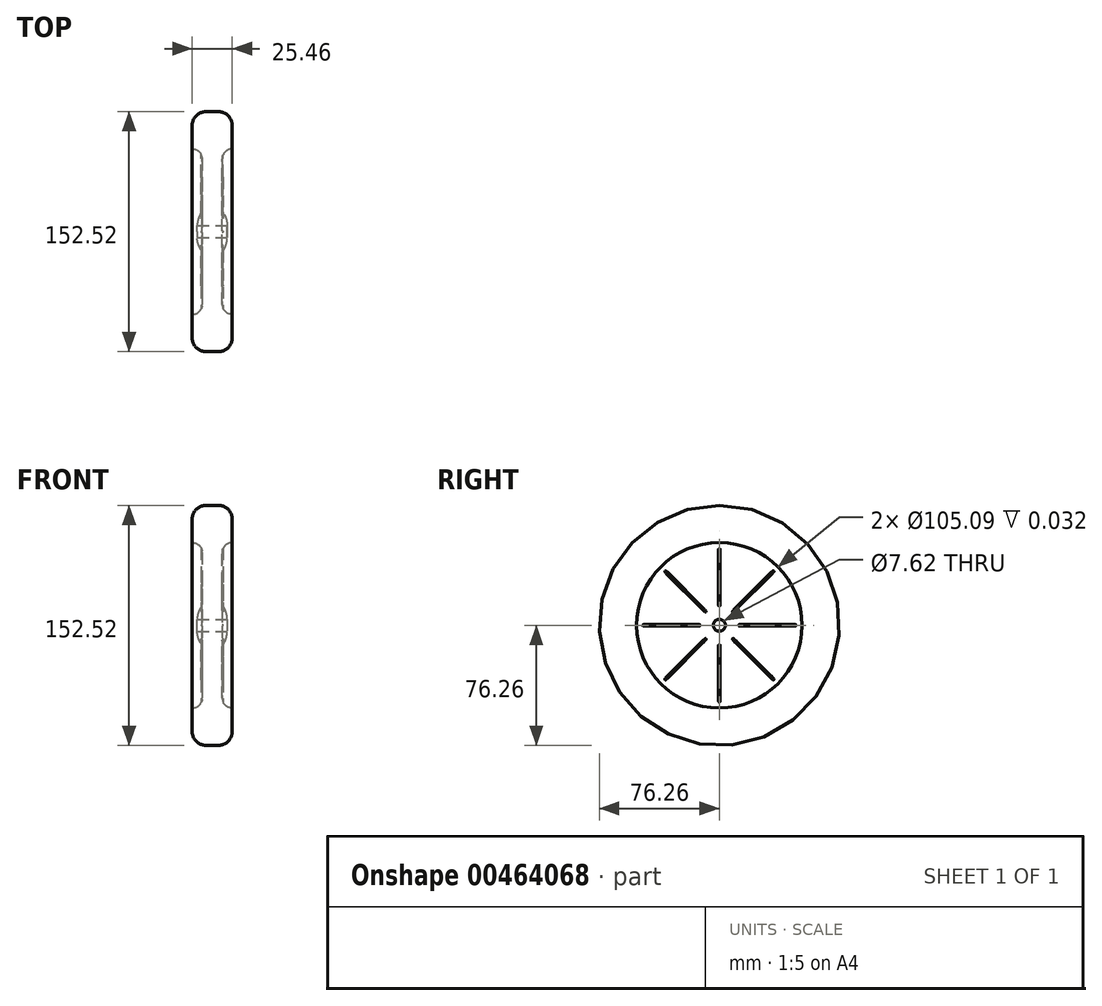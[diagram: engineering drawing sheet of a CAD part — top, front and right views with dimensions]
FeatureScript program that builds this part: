
annotation { "Feature Type Name" : "Feature", "Feature Type Description" : "" }
export const myFeature = defineFeature(function(context is Context, id is Id, definition is map)
    precondition{}
    {
        {
            var Q0;
            Q0=qCreatedBy(makeId("Top.planeOp"),FACE);
            var sketch = newSketch(context, id + "F0", { "sketchPlane" : qUnion([Q0])});
            skLineSegment(sketch, "E0", {"start": v(-6.3, -52.55) * mm, "end": v(-6.3, -12.74) * mm});
            skLineSegment(sketch, "E1", {"start": v(6.35, -12.7) * mm, "end": v(6.35, -52.55) * mm});
            skLineSegment(sketch, "E2", {"start": v(-9.53, 0) * mm, "end": v(-9.53, -3.81) * mm});
            skArc(sketch, "E3", {"start": v(-9.53, -3.81) * mm, "mid": v(-8.7, -8.56) * mm, "end": v(-6.3, -12.74) * mm});
            skArc(sketch, "E4", {"start": v(-12.7, 0) * mm, "mid": v(-11.82, -2.5) * mm, "end": v(-9.53, -3.8) * mm});
            skArc(sketch, "E5.MirrorCS", {"start": v(9.53, -3.81) * mm, "mid": v(8.7, -8.53) * mm, "end": v(6.35, -12.7) * mm});
            skArc(sketch, "E6.MirrorCS", {"start": v(12.7, 0) * mm, "mid": v(11.82, -2.5) * mm, "end": v(9.53, -3.8) * mm});
            skLineSegment(sketch, "E7", {"start": v(-12.7, 0) * mm, "end": v(12.7, 0) * mm});
            skLineSegment(sketch, "E8", {"start": v(12.73, -63.55) * mm, "end": v(12.73, -52.55) * mm});
            skLineSegment(sketch, "E9", {"start": v(12.73, -52.55) * mm, "end": v(6.35, -52.55) * mm});
            skLineSegment(sketch, "E10", {"start": v(12.73, -63.55) * mm, "end": v(12.73, -76.26) * mm});
            skLineSegment(sketch, "E11", {"start": v(-6.3, -52.55) * mm, "end": v(-12.73, -52.55) * mm});
            skLineSegment(sketch, "E12", {"start": v(-12.73, -52.55) * mm, "end": v(-12.73, -76.24) * mm});
            skLineSegment(sketch, "E13", {"start": v(-12.73, -76.24) * mm, "end": v(12.73, -76.26) * mm});
            skSolve(sketch);
        }
        {
            var Q0;
            Q0=makeQuery(id+"F0.imprint","IMPRINT",FACE,{"disambiguationData":[TD([[makeQuery(id+"F0.imprint","IMPRINT",EDGE,{"derivedFrom":sQuery(id+"F0.wireOp",EDGE,"E0")}),-1.0]])]});
            var Q1;
            {var subQ0=sQuery(id+"F0.wireOp",EDGE,"6V25OecG-Z0nX-RHxG-JKtg-aJSisBqB9ty6");var subQ1=makeQuery(id+"F0.imprint","INTERSECT",VERTEX,{"derivedFrom":[subQ0,sQuery(id+"F0.wireOp",EDGE,"s2MWHd5B-Butg-I8NC-5foa-pCvdFhJTHkwg")]});Q1=makeQuery(id+"F0.imprint","IMPRINT",FACE,{"disambiguationData":[TD([[makeQuery(id+"F0.imprint","IMPRINT",EDGE,{"disambiguationData":[TD([[subQ1,1.0]])],"derivedFrom":subQ0}),1.0]])]});}
            var Q2;
            Q2=makeQuery(id+"F0.imprint","IMPRINT",FACE,{"disambiguationData":[TD([[makeQuery(id+"F0.imprint","IMPRINT",EDGE,{"derivedFrom":sQuery(id+"F0.wireOp",EDGE,"wWwMu1eG-bIHq-Cr3w-0RTv-qLqCbcrmc8dO")}),1.0]])]});
            var Q3;
            Q3=makeQuery(id+"F0.imprint","IMPRINT",FACE,{"disambiguationData":[TD([[makeQuery(id+"F0.imprint","IMPRINT",EDGE,{"derivedFrom":sQuery(id+"F0.wireOp",EDGE,"6V25OecG-Z0nX-RHxG-JKtg-aJSisBqB9ty6")}),1.0]])]});
            var Q4;
            {var subQ0=sQuery(id+"F0.wireOp",EDGE,"E2");Q4=makeQuery(id+"F0.imprint","IMPRINT",FACE,{"disambiguationData":[TD([[makeQuery(id+"F0.imprint","IMPRINT",EDGE,{"derivedFrom":subQ0}),-1.0]])]});}
            var Q5;
            Q5=sQuery(id+"F0.wireOp",EDGE,"E7");
            revolve(context, id + "F1", {"entities" : qUnion([Q0, Q1, Q2, Q3, Q4]), "axis" : qUnion([Q5]), "revolveType" : RevolveType.FULL});
        }
        {
            var Q0;
            Q0=makeQuery(id+"F1.opRevolve","SWEPT_EDGE",EDGE,{"disambiguationData":[OSD([sQuery(id+"F0.wireOp",EDGE,"6V25OecG-Z0nX-RHxG-JKtg-aJSisBqB9ty6"),sQuery(id+"F0.wireOp",EDGE,"E1")])]});
            var Q1;
            Q1=makeQuery(id+"F1.opRevolve","SWEPT_EDGE",EDGE,{"disambiguationData":[OSD([sQuery(id+"F0.wireOp",EDGE,"6V25OecG-Z0nX-RHxG-JKtg-aJSisBqB9ty6"),sQuery(id+"F0.wireOp",EDGE,"E0")])]});
            fillet(context, id + "F2", {"entities" : qUnion([Q0, Q1]), "radius" : 6.35 * mm, "tangentPropagation" : true, "allowEdgeOverflow" : false});
        }
        {
            var Q0;
            Q0=makeQuery(id+"F1.opRevolve","SWEPT_FACE",FACE,{"disambiguationData":[OSD([sQuery(id+"F0.wireOp",EDGE,"E0")])]});
            var sketch = newSketch(context, id + "F3", { "sketchPlane" : qUnion([Q0])});
            skLineSegment(sketch, "E14", {"start": v(0, 0) * mm, "end": v(-46.2, 0) * mm});
            skLineSegment(sketch, "E15", {"start": v(0, 0) * mm, "end": v(0, 0.5) * mm});
            skLineSegment(sketch, "E16", {"start": v(-46.2, 0.5) * mm, "end": v(-46.2, 0) * mm});
            skLineSegment(sketch, "E17.MirrorCS", {"start": v(0, -0.5) * mm, "end": v(-46.2, -0.5) * mm});
            skLineSegment(sketch, "E18.MirrorCS", {"start": v(-46.2, -0.5) * mm, "end": v(-46.2, 0) * mm});
            skLineSegment(sketch, "E19.MirrorCS", {"start": v(0, 0) * mm, "end": v(0, -0.5) * mm});
            skLineSegment(sketch, "E20.1.4", {"start": v(0, 0) * mm, "end": v(-0.36, 0.36) * mm});
            skLineSegment(sketch, "E20.1.5", {"start": v(0, 0) * mm, "end": v(0.36, -0.36) * mm});
            skLineSegment(sketch, "E20.2.4", {"start": v(0, 0) * mm, "end": v(-0.5, 0) * mm});
            skLineSegment(sketch, "E20.2.5", {"start": v(0, 0) * mm, "end": v(0.5, 0) * mm});
            skLineSegment(sketch, "E20.3.4", {"start": v(0, 0) * mm, "end": v(-0.36, -0.36) * mm});
            skLineSegment(sketch, "E20.3.5", {"start": v(0, 0) * mm, "end": v(0.36, 0.36) * mm});
            skLineSegment(sketch, "E20.5.4", {"start": v(0, 0) * mm, "end": v(0.36, -0.36) * mm});
            skLineSegment(sketch, "E20.5.5", {"start": v(0, 0) * mm, "end": v(-0.36, 0.36) * mm});
            skLineSegment(sketch, "E20.6.4", {"start": v(0, 0) * mm, "end": v(0.5, 0) * mm});
            skLineSegment(sketch, "E20.6.5", {"start": v(0, 0) * mm, "end": v(-0.5, 0) * mm});
            skLineSegment(sketch, "E20.7.4", {"start": v(0, 0) * mm, "end": v(0.36, 0.36) * mm});
            skLineSegment(sketch, "E20.7.5", {"start": v(0, 0) * mm, "end": v(-0.36, -0.36) * mm});
            skPoint(sketch, "E20.center", {"position": v(0, 0) * mm});
            skLineSegment(sketch, "E21", {"start": v(0, 0.5) * mm, "end": v(-49.43, 0.5) * mm});
            skLineSegment(sketch, "E22", {"start": v(-49.43, 0.5) * mm, "end": v(-49.43, -0.5) * mm});
            skLineSegment(sketch, "E23", {"start": v(-49.43, -0.5) * mm, "end": v(-46.2, -0.5) * mm});
            skLineSegment(sketch, "E24.1.0", {"start": v(-0.36, 0.36) * mm, "end": v(-35.31, -34.6) * mm});
            skLineSegment(sketch, "E24.1.1", {"start": v(0.36, -0.36) * mm, "end": v(-32.3, -33.02) * mm});
            skLineSegment(sketch, "E24.1.2", {"start": v(-34.6, -35.31) * mm, "end": v(-32.3, -33.02) * mm});
            skLineSegment(sketch, "E24.1.3", {"start": v(-35.31, -34.6) * mm, "end": v(-34.6, -35.31) * mm});
            skLineSegment(sketch, "E24.2.0", {"start": v(-0.5, 0) * mm, "end": v(-0.5, -49.43) * mm});
            skLineSegment(sketch, "E24.2.1", {"start": v(0.5, 0) * mm, "end": v(0.5, -46.2) * mm});
            skLineSegment(sketch, "E24.2.2", {"start": v(0.5, -49.43) * mm, "end": v(0.5, -46.2) * mm});
            skLineSegment(sketch, "E24.2.3", {"start": v(-0.5, -49.43) * mm, "end": v(0.5, -49.43) * mm});
            skLineSegment(sketch, "E24.3.0", {"start": v(-0.36, -0.36) * mm, "end": v(34.6, -35.31) * mm});
            skLineSegment(sketch, "E24.3.1", {"start": v(0.36, 0.36) * mm, "end": v(33.02, -32.3) * mm});
            skLineSegment(sketch, "E24.3.2", {"start": v(35.31, -34.6) * mm, "end": v(33.02, -32.3) * mm});
            skLineSegment(sketch, "E24.3.3", {"start": v(34.6, -35.31) * mm, "end": v(35.31, -34.6) * mm});
            skLineSegment(sketch, "E24.4.0", {"start": v(0, -0.5) * mm, "end": v(49.43, -0.5) * mm});
            skLineSegment(sketch, "E24.4.1", {"start": v(0, 0.5) * mm, "end": v(46.2, 0.5) * mm});
            skLineSegment(sketch, "E24.4.2", {"start": v(49.43, 0.5) * mm, "end": v(46.2, 0.5) * mm});
            skLineSegment(sketch, "E24.4.3", {"start": v(49.43, -0.5) * mm, "end": v(49.43, 0.5) * mm});
            skLineSegment(sketch, "E24.5.0", {"start": v(0.36, -0.36) * mm, "end": v(35.31, 34.6) * mm});
            skLineSegment(sketch, "E24.5.1", {"start": v(-0.36, 0.36) * mm, "end": v(32.3, 33.02) * mm});
            skLineSegment(sketch, "E24.5.2", {"start": v(34.6, 35.31) * mm, "end": v(32.3, 33.02) * mm});
            skLineSegment(sketch, "E24.5.3", {"start": v(35.31, 34.6) * mm, "end": v(34.6, 35.31) * mm});
            skLineSegment(sketch, "E24.6.0", {"start": v(0.5, 0) * mm, "end": v(0.5, 49.43) * mm});
            skLineSegment(sketch, "E24.6.1", {"start": v(-0.5, 0) * mm, "end": v(-0.5, 46.2) * mm});
            skLineSegment(sketch, "E24.6.2", {"start": v(-0.5, 49.43) * mm, "end": v(-0.5, 46.2) * mm});
            skLineSegment(sketch, "E24.6.3", {"start": v(0.5, 49.43) * mm, "end": v(-0.5, 49.43) * mm});
            skLineSegment(sketch, "E24.7.0", {"start": v(0.36, 0.36) * mm, "end": v(-34.6, 35.31) * mm});
            skLineSegment(sketch, "E24.7.1", {"start": v(-0.36, -0.36) * mm, "end": v(-33.02, 32.3) * mm});
            skLineSegment(sketch, "E24.7.2", {"start": v(-35.31, 34.6) * mm, "end": v(-33.02, 32.3) * mm});
            skLineSegment(sketch, "E24.7.3", {"start": v(-34.6, 35.31) * mm, "end": v(-35.31, 34.6) * mm});
            skSolve(sketch);
        }
        {
            var Q0;
            Q0 = qSketchRegion(id + "F3", true);
            extrude(context, id + "F4", {"entities" : qUnion([Q0]), "operationType" : NewBodyOperationType.ADD, "depth" : 0.64 * mm, "offsetDistance" : 25.4 * mm});
        }
        {
            var Q0;
            {var subQ0=sQuery(id+"F3.wireOp",EDGE,"E24.7.0");var subQ1=sQuery(id+"F0.wireOp",EDGE,"E0");var subQ2=makeQuery(id+"F1.opRevolve","SWEPT_FACE",FACE,{"disambiguationData":[OSD([subQ1])]});var subQ3=makeQuery(id+"F3.imprint","INTERSECT",VERTEX,{"derivedFrom":[makeQuery(id+"F2.opFillet","BLEND_EDGE",EDGE,{"blendedFrom":[makeQuery(id+"F1.opRevolve","SWEPT_EDGE",EDGE,{"disambiguationData":[OSD([subQ1,sQuery(id+"F0.wireOp",EDGE,"E11")])]}),subQ2],"blendedInto":[subQ2]}),subQ0]});Q0=makeQuery(id+"F4.opExtrude","CAP_EDGE",EDGE,{"disambiguationData":[OSD([subQ0]),TDD([makeQuery(id+"F3.imprint","IMPRINT",EDGE,{"disambiguationData":[TD([[makeQuery(id+"F3.imprint","INTERSECT",VERTEX,{"derivedFrom":[sQuery(id+"F3.wireOp",EDGE,"E24.6.1"),subQ0]}),-1.0]])],"derivedFrom":subQ0}),makeQuery(id+"F3.imprint","IMPRINT",EDGE,{"disambiguationData":[TD([[subQ3,1.0]])],"derivedFrom":subQ0}),makeQuery(id+"F3.imprint","IMPRINT",EDGE,{"disambiguationData":[TD([[makeQuery(id+"F3.imprint","INTERSECT",VERTEX,{"derivedFrom":[subQ0,sQuery(id+"F3.wireOp",EDGE,"E24.7.3")]}),1.0]])],"derivedFrom":subQ0})])],"isStart":false});}
            var Q1;
            {var subQ0=sQuery(id+"F3.wireOp",EDGE,"E24.6.0");var subQ1=sQuery(id+"F0.wireOp",EDGE,"E0");var subQ2=makeQuery(id+"F1.opRevolve","SWEPT_FACE",FACE,{"disambiguationData":[OSD([subQ1])]});var subQ3=makeQuery(id+"F3.imprint","INTERSECT",VERTEX,{"derivedFrom":[makeQuery(id+"F2.opFillet","BLEND_EDGE",EDGE,{"blendedFrom":[makeQuery(id+"F1.opRevolve","SWEPT_EDGE",EDGE,{"disambiguationData":[OSD([subQ1,sQuery(id+"F0.wireOp",EDGE,"E11")])]}),subQ2],"blendedInto":[subQ2]}),subQ0]});Q1=makeQuery(id+"F4.opExtrude","CAP_EDGE",EDGE,{"disambiguationData":[OSD([subQ0]),TDD([makeQuery(id+"F3.imprint","IMPRINT",EDGE,{"disambiguationData":[TD([[makeQuery(id+"F3.imprint","INTERSECT",VERTEX,{"derivedFrom":[sQuery(id+"F3.wireOp",EDGE,"E24.5.1"),subQ0]}),-1.0]])],"derivedFrom":subQ0}),makeQuery(id+"F3.imprint","IMPRINT",EDGE,{"disambiguationData":[TD([[subQ3,1.0]])],"derivedFrom":subQ0}),makeQuery(id+"F3.imprint","IMPRINT",EDGE,{"disambiguationData":[TD([[makeQuery(id+"F3.imprint","INTERSECT",VERTEX,{"derivedFrom":[subQ0,sQuery(id+"F3.wireOp",EDGE,"E24.6.3")]}),1.0]])],"derivedFrom":subQ0})])],"isStart":false});}
            var Q2;
            {var subQ0=sQuery(id+"F3.wireOp",EDGE,"E24.5.0");var subQ1=sQuery(id+"F0.wireOp",EDGE,"E0");var subQ2=makeQuery(id+"F1.opRevolve","SWEPT_FACE",FACE,{"disambiguationData":[OSD([subQ1])]});var subQ3=makeQuery(id+"F3.imprint","INTERSECT",VERTEX,{"derivedFrom":[makeQuery(id+"F2.opFillet","BLEND_EDGE",EDGE,{"blendedFrom":[makeQuery(id+"F1.opRevolve","SWEPT_EDGE",EDGE,{"disambiguationData":[OSD([subQ1,sQuery(id+"F0.wireOp",EDGE,"E11")])]}),subQ2],"blendedInto":[subQ2]}),subQ0]});Q2=makeQuery(id+"F4.opExtrude","CAP_EDGE",EDGE,{"disambiguationData":[OSD([subQ0]),TDD([makeQuery(id+"F3.imprint","IMPRINT",EDGE,{"disambiguationData":[TD([[makeQuery(id+"F3.imprint","INTERSECT",VERTEX,{"derivedFrom":[sQuery(id+"F3.wireOp",EDGE,"E24.4.1"),subQ0]}),-1.0]])],"derivedFrom":subQ0}),makeQuery(id+"F3.imprint","IMPRINT",EDGE,{"disambiguationData":[TD([[subQ3,1.0]])],"derivedFrom":subQ0}),makeQuery(id+"F3.imprint","IMPRINT",EDGE,{"disambiguationData":[TD([[makeQuery(id+"F3.imprint","INTERSECT",VERTEX,{"derivedFrom":[subQ0,sQuery(id+"F3.wireOp",EDGE,"E24.5.3")]}),1.0]])],"derivedFrom":subQ0})])],"isStart":false});}
            var Q3;
            Q3=makeQuery(id+"F4.opExtrude","CAP_EDGE",EDGE,{"disambiguationData":[OSD([sQuery(id+"F3.wireOp",EDGE,"E17.MirrorCS"),sQuery(id+"F3.wireOp",EDGE,"E23")])],"isStart":false});
            var Q4;
            {var subQ0=sQuery(id+"F3.wireOp",EDGE,"E21");var subQ1=sQuery(id+"F0.wireOp",EDGE,"E0");var subQ2=makeQuery(id+"F1.opRevolve","SWEPT_FACE",FACE,{"disambiguationData":[OSD([subQ1])]});var subQ4=makeQuery(id+"F3.imprint","INTERSECT",VERTEX,{"derivedFrom":[makeQuery(id+"F2.opFillet","BLEND_EDGE",EDGE,{"blendedFrom":[makeQuery(id+"F1.opRevolve","SWEPT_EDGE",EDGE,{"disambiguationData":[OSD([subQ1,sQuery(id+"F0.wireOp",EDGE,"E3")])]}),subQ2],"blendedInto":[subQ2]}),subQ0]});Q4=makeQuery(id+"F4.opExtrude","CAP_EDGE",EDGE,{"disambiguationData":[OSD([subQ0]),TDD([makeQuery(id+"F3.imprint","IMPRINT",EDGE,{"disambiguationData":[TD([[makeQuery(id+"F3.imprint","INTERSECT",VERTEX,{"derivedFrom":[subQ0,sQuery(id+"F3.wireOp",EDGE,"E24.7.1")]}),-1.0]])],"derivedFrom":subQ0}),makeQuery(id+"F3.imprint","IMPRINT",EDGE,{"disambiguationData":[TD([[subQ4,-1.0]])],"derivedFrom":subQ0}),makeQuery(id+"F3.imprint","IMPRINT",EDGE,{"disambiguationData":[TD([[makeQuery(id+"F3.imprint","INTERSECT",VERTEX,{"derivedFrom":[subQ0,sQuery(id+"F3.wireOp",EDGE,"E22")]}),1.0]])],"derivedFrom":subQ0})])],"isStart":false});}
            var Q5;
            Q5=makeQuery(id+"F4.opExtrude","CAP_EDGE",EDGE,{"disambiguationData":[OSD([sQuery(id+"F3.wireOp",EDGE,"E24.6.1"),sQuery(id+"F3.wireOp",EDGE,"E24.6.2")])],"isStart":false});
            var Q6;
            Q6=makeQuery(id+"F4.opExtrude","CAP_EDGE",EDGE,{"disambiguationData":[OSD([sQuery(id+"F3.wireOp",EDGE,"E24.5.1"),sQuery(id+"F3.wireOp",EDGE,"E24.5.2")])],"isStart":false});
            var Q7;
            Q7=makeQuery(id+"F4.opExtrude","CAP_EDGE",EDGE,{"disambiguationData":[OSD([sQuery(id+"F3.wireOp",EDGE,"E24.7.1"),sQuery(id+"F3.wireOp",EDGE,"E24.7.2")])],"isStart":false});
            var Q8;
            Q8=makeQuery(id+"F4.opExtrude","CAP_EDGE",EDGE,{"disambiguationData":[OSD([sQuery(id+"F3.wireOp",EDGE,"E24.4.1"),sQuery(id+"F3.wireOp",EDGE,"E24.4.2")])],"isStart":false});
            var Q9;
            {var subQ0=sQuery(id+"F3.wireOp",EDGE,"E24.4.0");var subQ1=sQuery(id+"F0.wireOp",EDGE,"E0");var subQ2=makeQuery(id+"F1.opRevolve","SWEPT_FACE",FACE,{"disambiguationData":[OSD([subQ1])]});var subQ3=makeQuery(id+"F3.imprint","INTERSECT",VERTEX,{"derivedFrom":[makeQuery(id+"F2.opFillet","BLEND_EDGE",EDGE,{"blendedFrom":[makeQuery(id+"F1.opRevolve","SWEPT_EDGE",EDGE,{"disambiguationData":[OSD([subQ1,sQuery(id+"F0.wireOp",EDGE,"E11")])]}),subQ2],"blendedInto":[subQ2]}),subQ0]});Q9=makeQuery(id+"F4.opExtrude","CAP_EDGE",EDGE,{"disambiguationData":[OSD([subQ0]),TDD([makeQuery(id+"F3.imprint","IMPRINT",EDGE,{"disambiguationData":[TD([[makeQuery(id+"F3.imprint","INTERSECT",VERTEX,{"derivedFrom":[sQuery(id+"F3.wireOp",EDGE,"E24.3.1"),subQ0]}),-1.0]])],"derivedFrom":subQ0}),makeQuery(id+"F3.imprint","IMPRINT",EDGE,{"disambiguationData":[TD([[subQ3,1.0]])],"derivedFrom":subQ0}),makeQuery(id+"F3.imprint","IMPRINT",EDGE,{"disambiguationData":[TD([[makeQuery(id+"F3.imprint","INTERSECT",VERTEX,{"derivedFrom":[subQ0,sQuery(id+"F3.wireOp",EDGE,"E24.4.3")]}),1.0]])],"derivedFrom":subQ0})])],"isStart":false});}
            var Q10;
            {var subQ0=sQuery(id+"F3.wireOp",EDGE,"E24.3.0");var subQ1=sQuery(id+"F0.wireOp",EDGE,"E0");var subQ2=makeQuery(id+"F1.opRevolve","SWEPT_FACE",FACE,{"disambiguationData":[OSD([subQ1])]});var subQ3=makeQuery(id+"F3.imprint","INTERSECT",VERTEX,{"derivedFrom":[makeQuery(id+"F2.opFillet","BLEND_EDGE",EDGE,{"blendedFrom":[makeQuery(id+"F1.opRevolve","SWEPT_EDGE",EDGE,{"disambiguationData":[OSD([subQ1,sQuery(id+"F0.wireOp",EDGE,"E11")])]}),subQ2],"blendedInto":[subQ2]}),subQ0]});Q10=makeQuery(id+"F4.opExtrude","CAP_EDGE",EDGE,{"disambiguationData":[OSD([subQ0]),TDD([makeQuery(id+"F3.imprint","IMPRINT",EDGE,{"disambiguationData":[TD([[makeQuery(id+"F3.imprint","INTERSECT",VERTEX,{"derivedFrom":[sQuery(id+"F3.wireOp",EDGE,"E24.2.1"),subQ0]}),-1.0]])],"derivedFrom":subQ0}),makeQuery(id+"F3.imprint","IMPRINT",EDGE,{"disambiguationData":[TD([[subQ3,1.0]])],"derivedFrom":subQ0}),makeQuery(id+"F3.imprint","IMPRINT",EDGE,{"disambiguationData":[TD([[makeQuery(id+"F3.imprint","INTERSECT",VERTEX,{"derivedFrom":[subQ0,sQuery(id+"F3.wireOp",EDGE,"E24.3.3")]}),1.0]])],"derivedFrom":subQ0})])],"isStart":false});}
            var Q11;
            Q11=makeQuery(id+"F4.opExtrude","CAP_EDGE",EDGE,{"disambiguationData":[OSD([sQuery(id+"F3.wireOp",EDGE,"E24.3.1"),sQuery(id+"F3.wireOp",EDGE,"E24.3.2")])],"isStart":false});
            var Q12;
            Q12=makeQuery(id+"F4.opExtrude","CAP_EDGE",EDGE,{"disambiguationData":[OSD([sQuery(id+"F3.wireOp",EDGE,"E24.2.1"),sQuery(id+"F3.wireOp",EDGE,"E24.2.2")])],"isStart":false});
            var Q13;
            {var subQ0=sQuery(id+"F3.wireOp",EDGE,"E24.2.0");var subQ1=sQuery(id+"F0.wireOp",EDGE,"E0");var subQ2=makeQuery(id+"F1.opRevolve","SWEPT_FACE",FACE,{"disambiguationData":[OSD([subQ1])]});var subQ3=makeQuery(id+"F3.imprint","INTERSECT",VERTEX,{"derivedFrom":[makeQuery(id+"F2.opFillet","BLEND_EDGE",EDGE,{"blendedFrom":[makeQuery(id+"F1.opRevolve","SWEPT_EDGE",EDGE,{"disambiguationData":[OSD([subQ1,sQuery(id+"F0.wireOp",EDGE,"E11")])]}),subQ2],"blendedInto":[subQ2]}),subQ0]});Q13=makeQuery(id+"F4.opExtrude","CAP_EDGE",EDGE,{"disambiguationData":[OSD([subQ0]),TDD([makeQuery(id+"F3.imprint","IMPRINT",EDGE,{"disambiguationData":[TD([[makeQuery(id+"F3.imprint","INTERSECT",VERTEX,{"derivedFrom":[sQuery(id+"F3.wireOp",EDGE,"E24.1.1"),subQ0]}),-1.0]])],"derivedFrom":subQ0}),makeQuery(id+"F3.imprint","IMPRINT",EDGE,{"disambiguationData":[TD([[subQ3,1.0]])],"derivedFrom":subQ0}),makeQuery(id+"F3.imprint","IMPRINT",EDGE,{"disambiguationData":[TD([[makeQuery(id+"F3.imprint","INTERSECT",VERTEX,{"derivedFrom":[subQ0,sQuery(id+"F3.wireOp",EDGE,"E24.2.3")]}),1.0]])],"derivedFrom":subQ0})])],"isStart":false});}
            var Q14;
            Q14=makeQuery(id+"F4.opExtrude","CAP_EDGE",EDGE,{"disambiguationData":[OSD([sQuery(id+"F3.wireOp",EDGE,"E24.1.1"),sQuery(id+"F3.wireOp",EDGE,"E24.1.2")])],"isStart":false});
            var Q15;
            {var subQ0=sQuery(id+"F3.wireOp",EDGE,"E24.1.0");var subQ1=sQuery(id+"F0.wireOp",EDGE,"E0");var subQ2=makeQuery(id+"F1.opRevolve","SWEPT_FACE",FACE,{"disambiguationData":[OSD([subQ1])]});var subQ3=makeQuery(id+"F3.imprint","INTERSECT",VERTEX,{"derivedFrom":[makeQuery(id+"F2.opFillet","BLEND_EDGE",EDGE,{"blendedFrom":[makeQuery(id+"F1.opRevolve","SWEPT_EDGE",EDGE,{"disambiguationData":[OSD([subQ1,sQuery(id+"F0.wireOp",EDGE,"E11")])]}),subQ2],"blendedInto":[subQ2]}),subQ0]});Q15=makeQuery(id+"F4.opExtrude","CAP_EDGE",EDGE,{"disambiguationData":[OSD([subQ0]),TDD([makeQuery(id+"F3.imprint","IMPRINT",EDGE,{"disambiguationData":[TD([[makeQuery(id+"F3.imprint","INTERSECT",VERTEX,{"derivedFrom":[sQuery(id+"F3.wireOp",EDGE,"E17.MirrorCS"),subQ0]}),-1.0]])],"derivedFrom":subQ0}),makeQuery(id+"F3.imprint","IMPRINT",EDGE,{"disambiguationData":[TD([[subQ3,1.0]])],"derivedFrom":subQ0}),makeQuery(id+"F3.imprint","IMPRINT",EDGE,{"disambiguationData":[TD([[makeQuery(id+"F3.imprint","INTERSECT",VERTEX,{"derivedFrom":[subQ0,sQuery(id+"F3.wireOp",EDGE,"E24.1.3")]}),1.0]])],"derivedFrom":subQ0})])],"isStart":false});}
            fillet(context, id + "F5", {"entities" : qUnion([Q0, Q1, Q2, Q3, Q4, Q5, Q6, Q7, Q8, Q9, Q10, Q11, Q12, Q13, Q14, Q15]), "radius" : 0.5 * mm, "tangentPropagation" : true, "allowEdgeOverflow" : false});
        }
        {
            var Q0;
            Q0=makeQuery(id+"F1.opRevolve","SWEPT_BODY",BODY,{"disambiguationData":[OSD([sQuery(id+"F0.wireOp",EDGE,"6V25OecG-Z0nX-RHxG-JKtg-aJSisBqB9ty6"),sQuery(id+"F0.wireOp",EDGE,"E0"),sQuery(id+"F0.wireOp",EDGE,"E1"),sQuery(id+"F0.wireOp",EDGE,"E3"),sQuery(id+"F0.wireOp",EDGE,"E4"),sQuery(id+"F0.wireOp",EDGE,"E5.MirrorCS"),sQuery(id+"F0.wireOp",EDGE,"E6.MirrorCS"),sQuery(id+"F0.wireOp",EDGE,"E7")])]});
            var Q1;
            Q1=qCreatedBy(makeId("Right.planeOp"),FACE);
            mirror(context, id + "F6", {"operationType" : NewBodyOperationType.ADD, "entities" : qUnion([Q0]), "mirrorPlane" : qUnion([Q1])});
        }
        {
            var Q0;
            Q0=makeQuery(id+"F6.opPattern","COPY",EDGE,{"derivedFrom":makeQuery(id+"F1.opRevolve","SWEPT_EDGE",EDGE,{"disambiguationData":[OSD([sQuery(id+"F0.wireOp",EDGE,"E10"),sQuery(id+"F0.wireOp",EDGE,"r4c0vuP9-tLd9-AmIe-8Apj-uQWcLqrIjKn1")])]}),"instanceName":"1"});
            var Q1;
            Q1=makeQuery(id+"F1.opRevolve","SWEPT_EDGE",EDGE,{"disambiguationData":[OSD([sQuery(id+"F0.wireOp",EDGE,"E10"),sQuery(id+"F0.wireOp",EDGE,"r4c0vuP9-tLd9-AmIe-8Apj-uQWcLqrIjKn1")])]});
            fillet(context, id + "F7", {"entities" : qUnion([Q0, Q1]), "radius" : 8.9 * mm, "tangentPropagation" : true, "allowEdgeOverflow" : false});
        }
        {
            var Q0;
            Q0=qCreatedBy(makeId("Right.planeOp"),FACE);
            var sketch = newSketch(context, id + "F8", { "sketchPlane" : qUnion([Q0])});
            skCircle(sketch, "E25", {"center": v(0, 0) * mm, "radius": 3.81 * mm});
            skSolve(sketch);
        }
        {
            var Q0;
            Q0 = qSketchRegion(id + "F8", true);
            extrude(context, id + "F9", {"entities" : qUnion([Q0]), "operationType" : NewBodyOperationType.REMOVE, "oppositeDirection" : true, "depth" : 25.4 * mm, "offsetDistance" : 25.4 * mm, "hasSecondDirection" : true, "secondDirectionOppositeDirection" : false, "secondDirectionDepth" : 25.4 * mm});
        }
    });
